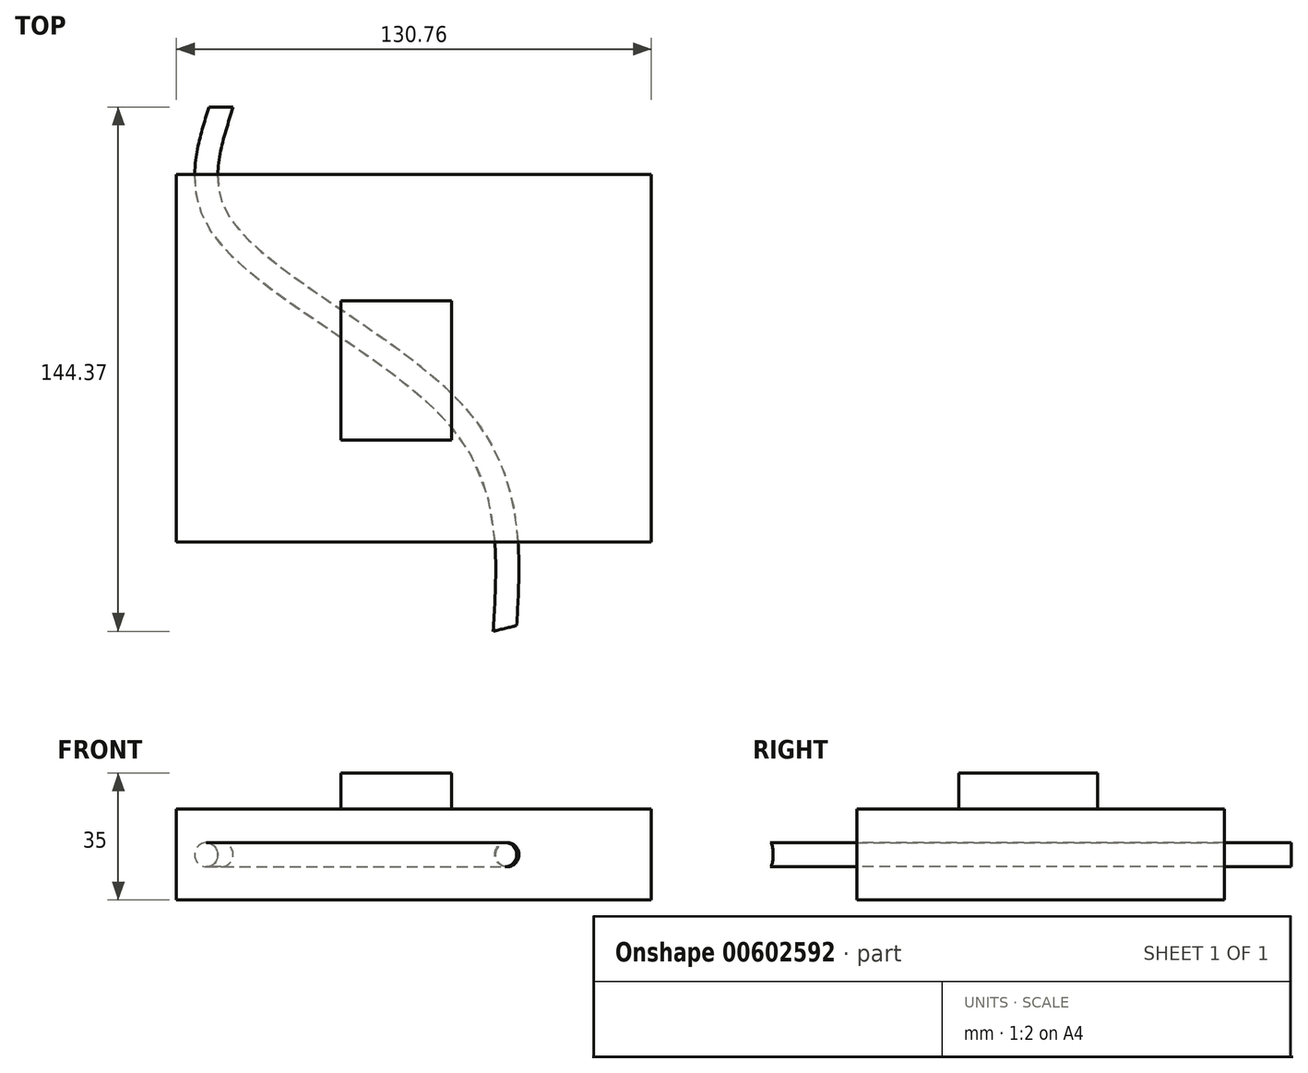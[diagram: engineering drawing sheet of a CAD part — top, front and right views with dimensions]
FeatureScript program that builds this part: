
annotation { "Feature Type Name" : "Feature", "Feature Type Description" : "" }
export const myFeature = defineFeature(function(context is Context, id is Id, definition is map)
    precondition{}
    {
        {
            var Q0;
            Q0=qCreatedBy(makeId("Top.planeOp"),FACE);
            var sketch = newSketch(context, id + "F0", { "sketchPlane" : qUnion([Q0])});
            skFitSpline(sketch, "E0", {"points": [v(-53.93, 69.14) * mm, v(-53.93, 36.35) * mm, v(13.1, -18.59) * mm, v(24.27, -74.63) * mm], "startDerivative": vector(-41.3, -130.5) * mm, "endDerivative": vector(-10.62, -175.57) * mm});
            skSolve(sketch);
        }
        {
            var Q0;
            Q0=qCreatedBy(makeId("Front.planeOp"),FACE);
            cPlane(context, id + "F1", {"entities" : qUnion([Q0]), "cplaneType" : CPlaneType.OFFSET, "offset" : 66.2 * mm, "oppositeDirection" : true, "width" : 150 * mm, "height" : 150 * mm});
        }
        {
            var Q0;
            Q0=qCreatedBy(id+"F1.planeOp",FACE);
            var sketch = newSketch(context, id + "F2", { "sketchPlane" : qUnion([Q0])});
            skCircle(sketch, "E1", {"center": v(-54, 0) * mm, "radius": 3.34 * mm});
            skSolve(sketch);
        }
        {
            var Q0;
            Q0=makeQuery(id+"F2.imprint","IMPRINT",FACE,{"disambiguationData":[TD([[makeQuery(id+"F2.imprint","IMPRINT",EDGE,{"derivedFrom":sQuery(id+"F2.wireOp",EDGE,"E1")}),1.0]])]});
            var Q1;
            Q1 = qConstructionFilter(qBodyType(qCreatedBy(id + "F0" ,EDGE), BodyType.WIRE), ConstructionObject.NO);
            sweep(context, id + "F3", {"profiles" : qUnion([Q0]), "path" : qUnion([Q1])});
        }
        {
            var Q0;
            Q0=qCreatedBy(makeId("Top.planeOp"),FACE);
            var sketch = newSketch(context, id + "F4", { "sketchPlane" : qUnion([Q0])});
            skLineSegment(sketch, "E2.bottom", {"start": v(-65.38, 50.6) * mm, "end": v(65.38, 50.6) * mm});
            skLineSegment(sketch, "E2.top", {"start": v(-65.38, -50.6) * mm, "end": v(65.38, -50.6) * mm});
            skLineSegment(sketch, "E2.left", {"start": v(-65.38, 50.6) * mm, "end": v(-65.38, -50.6) * mm});
            skLineSegment(sketch, "E2.right", {"start": v(65.38, 50.6) * mm, "end": v(65.38, -50.6) * mm});
            skPoint(sketch, "E2.middle", {"position": v(0, 0) * mm});
            skSolve(sketch);
        }
        {
            var Q0;
            Q0=makeQuery(id+"F4.imprint","IMPRINT",FACE,{"disambiguationData":[TD([[makeQuery(id+"F4.imprint","IMPRINT",EDGE,{"derivedFrom":sQuery(id+"F4.wireOp",EDGE,"E2.bottom")}),-1.0]])]});
            extrude(context, id + "F5", {"entities" : qUnion([Q0]), "depth" : 25 * mm, "offsetDistance" : 25 * mm, "symmetric" : true});
        }
        {
            var Q0;
            Q0=makeQuery(id+"F5.opExtrude","CAP_FACE",FACE,{"disambiguationData":[OSD([sQuery(id+"F4.wireOp",EDGE,"E2.bottom"),sQuery(id+"F4.wireOp",EDGE,"E2.top"),sQuery(id+"F4.wireOp",EDGE,"E2.left"),sQuery(id+"F4.wireOp",EDGE,"E2.right")])],"isStart":false});
            var sketch = newSketch(context, id + "F6", { "sketchPlane" : qUnion([Q0])});
            skLineSegment(sketch, "E3.bottom", {"start": v(-20.02, 15.75) * mm, "end": v(10.35, 15.75) * mm});
            skLineSegment(sketch, "E3.top", {"start": v(-20.02, -22.55) * mm, "end": v(10.35, -22.55) * mm});
            skLineSegment(sketch, "E3.left", {"start": v(-20.02, 15.75) * mm, "end": v(-20.02, -22.55) * mm});
            skLineSegment(sketch, "E3.right", {"start": v(10.35, 15.75) * mm, "end": v(10.35, -22.55) * mm});
            skPoint(sketch, "E3.middle", {"position": v(-4.84, -3.4) * mm});
            skSolve(sketch);
        }
        {
            var Q0;
            Q0=makeQuery(id+"F6.imprint","IMPRINT",FACE,{"disambiguationData":[TD([[makeQuery(id+"F6.imprint","IMPRINT",EDGE,{"derivedFrom":sQuery(id+"F6.wireOp",EDGE,"E3.bottom")}),-1.0]])]});
            extrude(context, id + "F7", {"entities" : qUnion([Q0]), "depth" : 10 * mm, "offsetDistance" : 25 * mm});
        }
        {
            var Q0;
            Q0=makeQuery(id+"F3.opSweep","SWEPT_BODY",BODY,{"disambiguationData":[OSD([sQuery(id+"F0.wireOp",EDGE,"E0"),sQuery(id+"F2.wireOp",EDGE,"E1")])]});
            var Q1;
            Q1=makeQuery(id+"F5.opExtrude","SWEPT_BODY",BODY,{"disambiguationData":[OSD([sQuery(id+"F4.wireOp",EDGE,"E2.bottom"),sQuery(id+"F4.wireOp",EDGE,"E2.top"),sQuery(id+"F4.wireOp",EDGE,"E2.left"),sQuery(id+"F4.wireOp",EDGE,"E2.right")])]});
            booleanBodies(context, id + "F8", {"operationType" : BooleanOperationType.SUBTRACTION, "tools" : qUnion([Q0]), "targets" : qUnion([Q1]), "keepTools" : true});
        }
    });
